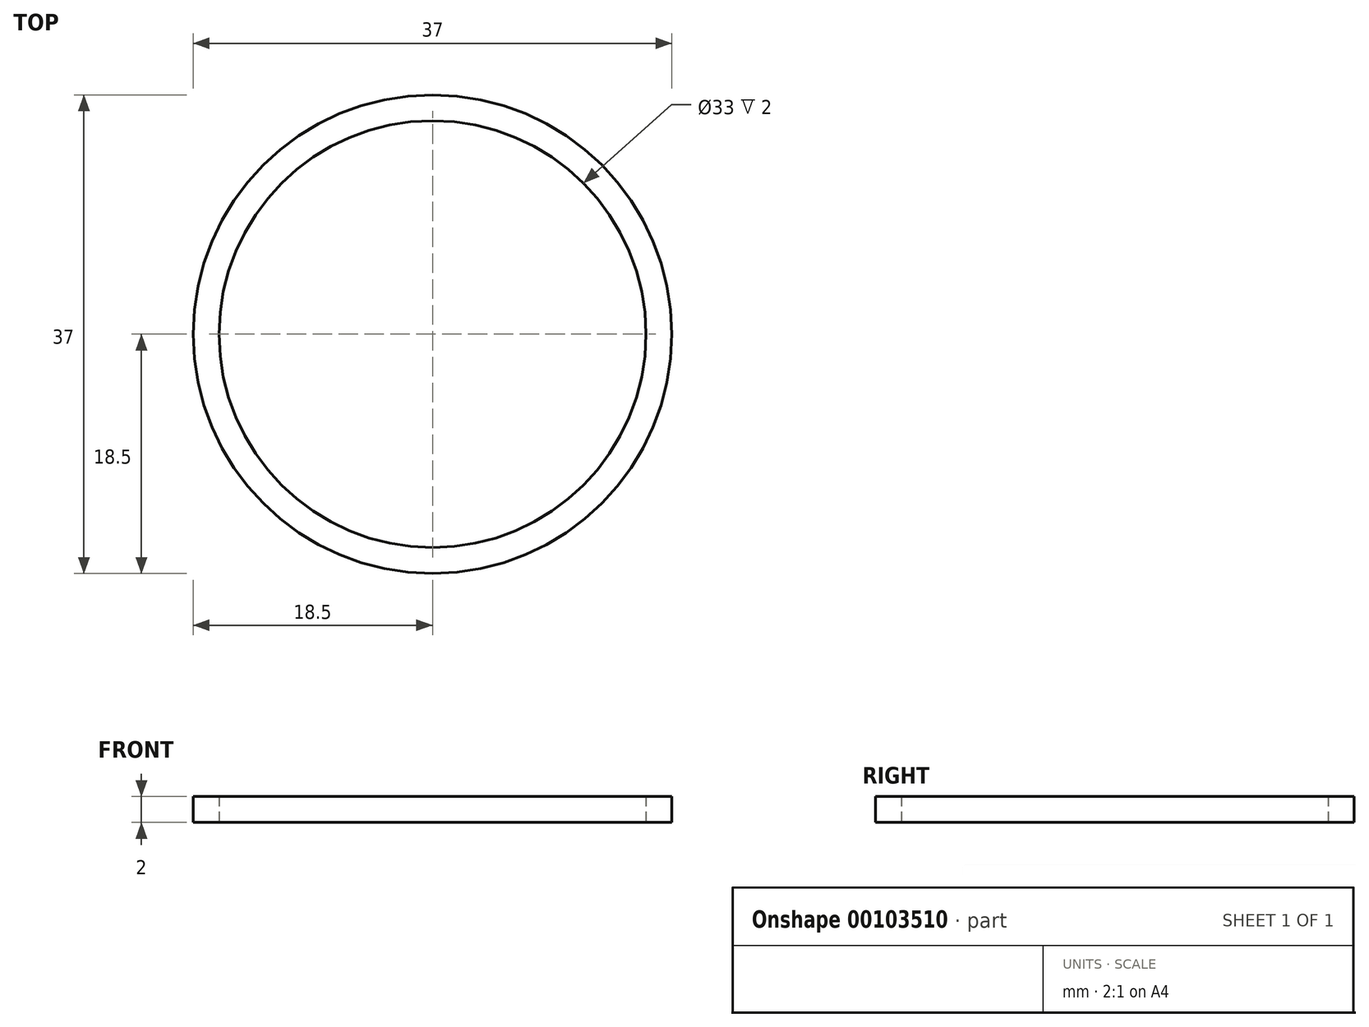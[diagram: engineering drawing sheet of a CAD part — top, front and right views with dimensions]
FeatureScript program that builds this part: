
annotation { "Feature Type Name" : "Feature", "Feature Type Description" : "" }
export const myFeature = defineFeature(function(context is Context, id is Id, definition is map)
    precondition{}
    {
        {
            var Q0;
            Q0=qCreatedBy(makeId("Top.planeOp"),FACE);
            var sketch = newSketch(context, id + "F0", { "sketchPlane" : qUnion([Q0])});
            skCircle(sketch, "E0", {"center": v(0, 0) * mm, "radius": 16.5 * mm});
            skCircle(sketch, "E1.0", {"center": v(0, 0) * mm, "radius": 18.5 * mm});
            skSolve(sketch);
        }
        {
            var Q0;
            Q0=makeQuery(id+"F0.imprint","IMPRINT",FACE,{"disambiguationData":[TD([[makeQuery(id+"F0.imprint","IMPRINT",EDGE,{"derivedFrom":sQuery(id+"F0.wireOp",EDGE,"E0")}),-1.0]])]});
            extrude(context, id + "F1", {"entities" : qUnion([Q0]), "depth" : 2 * mm});
        }
    });
